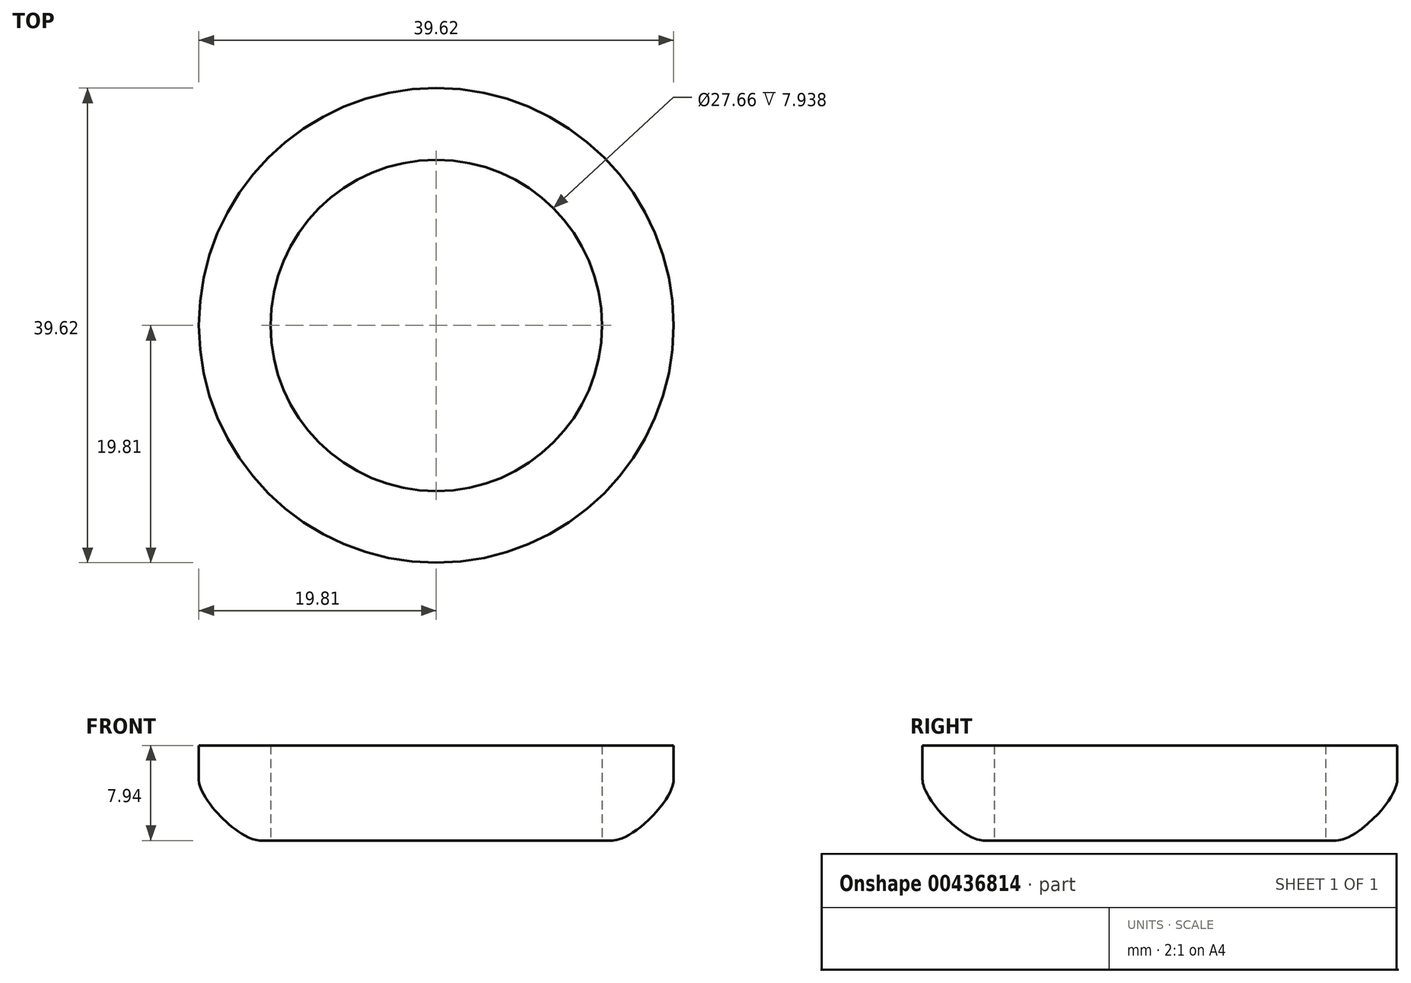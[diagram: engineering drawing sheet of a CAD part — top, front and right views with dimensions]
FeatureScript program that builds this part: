
annotation { "Feature Type Name" : "Feature", "Feature Type Description" : "" }
export const myFeature = defineFeature(function(context is Context, id is Id, definition is map)
    precondition{}
    {
        {
            var Q0;
            Q0=qCreatedBy(makeId("Top.planeOp"),FACE);
            var sketch = newSketch(context, id + "F0", { "sketchPlane" : qUnion([Q0])});
            skCircle(sketch, "E0", {"center": v(0, 0) * mm, "radius": 13.83 * mm});
            skCircle(sketch, "E1", {"center": v(0, 0) * mm, "radius": 19.81 * mm});
            skCircle(sketch, "E2", {"center": v(0, 0) * mm, "radius": 3.3 * mm});
            skPoint(sketch, "E3", {"position": v(0, 19.81) * mm});
            skLineSegment(sketch, "E4", {"start": v(0, 6.13) * mm, "end": v(0, 19.81) * mm});
            skSolve(sketch);
        }
        {
            var Q0;
            Q0=qSketchRegion(id+"F0",true);
            extrude(context, id + "F1", {"entities" : qUnion([Q0]), "depth" : 7.94 * mm});
        }
        {
            var Q0;
            Q0=qCreatedBy(makeId("Top.planeOp"),FACE);
            cPlane(context, id + "F2", {"entities" : qUnion([Q0]), "cplaneType" : CPlaneType.OFFSET, "offset" : 33.02 * mm, "width" : 152.4 * mm, "height" : 152.4 * mm});
        }
        {
            var Q0;
            Q0=qCreatedBy(id+"F2.planeOp",FACE);
            var sketch = newSketch(context, id + "F3", { "sketchPlane" : qUnion([Q0])});
            skCircle(sketch, "E5", {"center": v(0, 0) * mm, "radius": 6.5 * mm});
            skCircle(sketch, "E6", {"center": v(0, 0) * mm, "radius": 5.3 * mm});
            skPoint(sketch, "E7", {"position": v(-3.95, 3.52) * mm});
            skLineSegment(sketch, "E8", {"start": v(0, 5.3) * mm, "end": v(0, 0) * mm});
            skPoint(sketch, "E9", {"position": v(0, 6.5) * mm});
            skSolve(sketch);
        }
        {
            var Q0;
            Q0=makeQuery(id+"F1.opExtrude","CAP_EDGE",EDGE,{"disambiguationData":[OSD([sQuery(id+"F0.wireOp",EDGE,"E1")])],"isStart":true});
            fillet(context, id + "F4", {"entities" : qUnion([Q0]), "radius" : 5.08 * mm, "tangentPropagation" : true, "rho" : .25, "crossSection" : FilletCrossSection.CONIC, "allowEdgeOverflow" : false});
        }
        {
            var Q0;
            Q0=qCreatedBy(makeId("Top.planeOp"),FACE);
            cPlane(context, id + "F5", {"entities" : qUnion([Q0]), "cplaneType" : CPlaneType.OFFSET, "offset" : 7.94 * mm, "width" : 152.4 * mm, "height" : 152.4 * mm});
        }
        {
            var Q0;
            Q0=qCreatedBy(makeId("Right.planeOp"),FACE);
            var sketch = newSketch(context, id + "F6", { "sketchPlane" : qUnion([Q0])});
            skPoint(sketch, "E10", {"position": v(2, 33.02) * mm});
            skPoint(sketch, "E11", {"position": v(19.81, 7.94) * mm});
            skLineSegment(sketch, "E12", {"start": v(6.5, 33.02) * mm, "end": v(19.81, 7.94) * mm});
            skPoint(sketch, "E13", {"position": v(0, 33.02) * mm});
            skPoint(sketch, "E14", {"position": v(0, 7.94) * mm});
            skLineSegment(sketch, "E15", {"start": v(0, 7.94) * mm, "end": v(19.81, 7.94) * mm});
            skLineSegment(sketch, "E16", {"start": v(0, 33.02) * mm, "end": v(2, 33.02) * mm});
            skSolve(sketch);
        }
        {
            var Q0;
            Q0=qCreatedBy(makeId("Right.planeOp"),FACE);
            var sketch = newSketch(context, id + "F7", { "sketchPlane" : qUnion([Q0])});
            skLineSegment(sketch, "E17", {"start": v(0, 7.94) * mm, "end": v(0, 33.02) * mm});
            skSolve(sketch);
        }
        {
            var Q0;
            Q0=qSketchRegion(id+"F6",true);
            var Q1;
            Q1=qConstructionFilter(qBodyType(qCreatedBy(id+"F6",EDGE),BodyType.WIRE),ConstructionObject.NO);
            var Q2;
            Q2=sQuery(id+"F7.wireOp",EDGE,"E17");
            revolve(context, id + "F8", {"bodyType" : ToolBodyType.SURFACE, "operationType" : NewBodyOperationType.ADD, "entities" : qUnion([Q0]), "surfaceEntities" : qUnion([Q1]), "axis" : qUnion([Q2]), "revolveType" : RevolveType.FULL});
        }
        {
            var Q0;
            Q0=qCreatedBy(id+"F2.planeOp",FACE);
            cPlane(context, id + "F9", {"entities" : qUnion([Q0]), "cplaneType" : CPlaneType.OFFSET, "offset" : 39.37 * mm, "width" : 152.4 * mm, "height" : 152.4 * mm});
        }
        {
            var Q0;
            Q0=qCreatedBy(makeId("Right.planeOp"),FACE);
            var sketch = newSketch(context, id + "F10", { "sketchPlane" : qUnion([Q0])});
            skLineSegment(sketch, "E18", {"start": v(0, 33.05) * mm, "end": v(0, 72.39) * mm});
            skSolve(sketch);
        }
        {
            var Q0;
            Q0=qCreatedBy(makeId("Right.planeOp"),FACE);
            var sketch = newSketch(context, id + "F11", { "sketchPlane" : qUnion([Q0])});
            skLineSegment(sketch, "E19", {"start": v(6.5, 33.02) * mm, "end": v(6.47, 72.4) * mm});
            skSolve(sketch);
        }
        {
            var Q0;
            Q0=sQuery(id+"F11.wireOp",EDGE,"E19");
            var Q1;
            Q1=sQuery(id+"F10.wireOp",EDGE,"E18");
            revolve(context, id + "F12", {"bodyType" : ToolBodyType.SURFACE, "surfaceEntities" : qUnion([Q0]), "axis" : qUnion([Q1]), "revolveType" : RevolveType.FULL});
        }
        {
            var Q0;
            Q0=qCreatedBy(id+"F2.planeOp",FACE);
            var sketch = newSketch(context, id + "F13", { "sketchPlane" : qUnion([Q0])});
            skCircle(sketch, "E20", {"center": v(0, 0) * mm, "radius": 5.78 * mm});
            skSolve(sketch);
        }
        {
            var Q0;
            Q0 = qSketchRegion(id + "F13", true);
            extrude(context, id + "F14", {"entities" : qUnion([Q0]), "operationType" : NewBodyOperationType.REMOVE, "depth" : 40.64 * mm, "hasSecondDirection" : true, "secondDirectionOppositeDirection" : true, "secondDirectionDepth" : 40.64 * mm});
        }
    });
